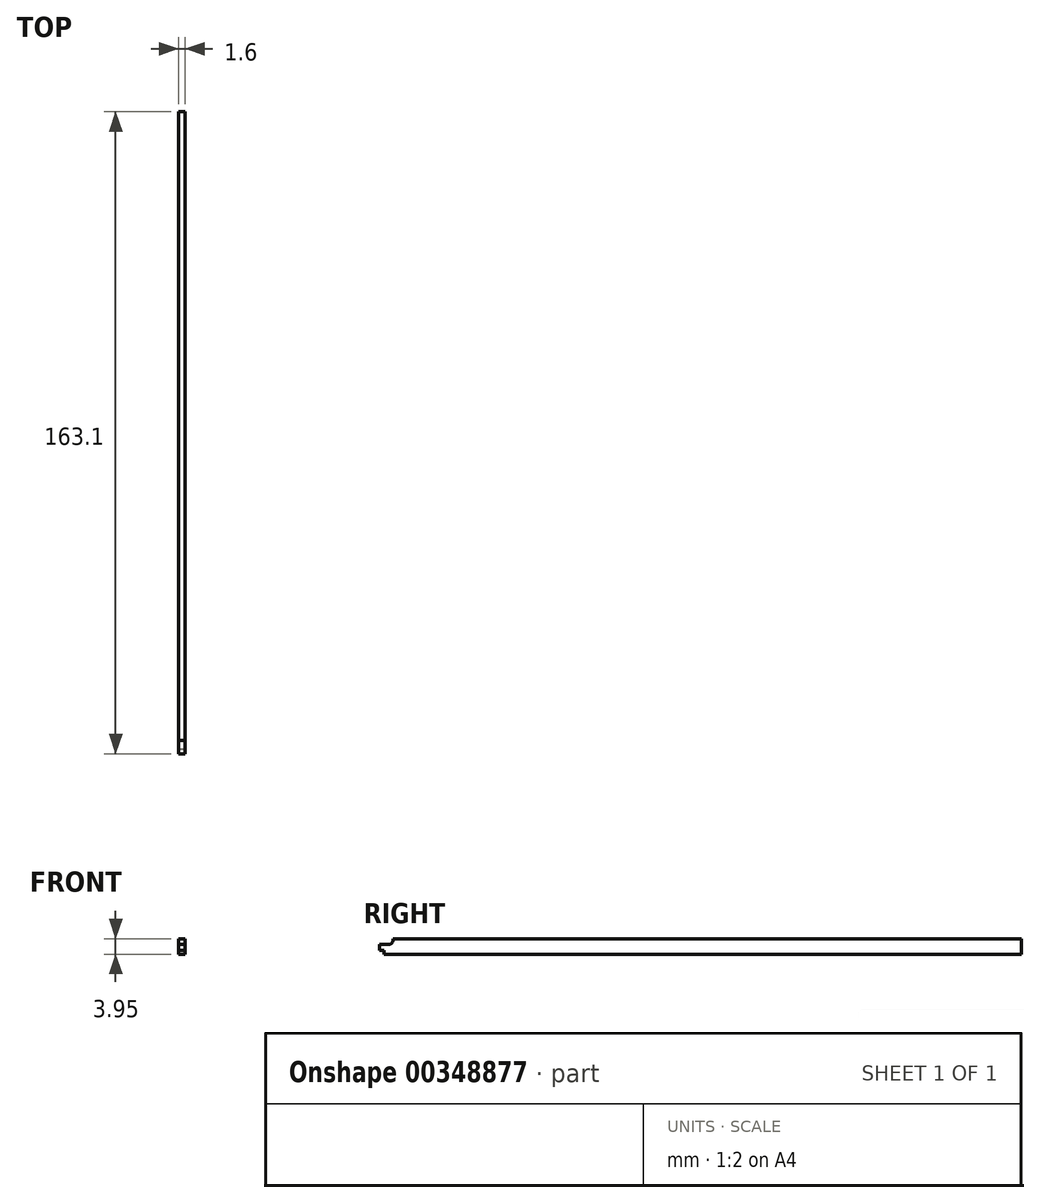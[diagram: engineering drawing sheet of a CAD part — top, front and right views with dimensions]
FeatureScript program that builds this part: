
annotation { "Feature Type Name" : "Feature", "Feature Type Description" : "" }
export const myFeature = defineFeature(function(context is Context, id is Id, definition is map)
    precondition{}
    {
        {
            var Q0;
            Q0=qCreatedBy(makeId("Front.planeOp"),FACE);
            var sketch = newSketch(context, id + "F0", { "sketchPlane" : qUnion([Q0])});
            skLineSegment(sketch, "E0.bottom", {"start": v(0, 0) * mm, "end": v(1.6, 0) * mm});
            skLineSegment(sketch, "E0.top", {"start": v(0, 3.95) * mm, "end": v(1.6, 3.95) * mm});
            skLineSegment(sketch, "E0.left", {"start": v(0, 0) * mm, "end": v(0, 3.95) * mm});
            skLineSegment(sketch, "E0.right", {"start": v(1.6, 0) * mm, "end": v(1.6, 3.95) * mm});
            skSolve(sketch);
        }
        {
            var Q0;
            Q0=qSketchRegion(id+"F0",true);
            extrude(context, id + "F1", {"entities" : qUnion([Q0]), "depth" : 163.1 * mm});
        }
        {
            var Q0;
            Q0=makeQuery(id+"F1.opExtrude","SWEPT_FACE",FACE,{"disambiguationData":[OSD([sQuery(id+"F0.wireOp",EDGE,"E0.right")])]});
            var sketch = newSketch(context, id + "F2", { "sketchPlane" : qUnion([Q0])});
            skLineSegment(sketch, "E1.bottom", {"start": v(-163.1, 3.95) * mm, "end": v(-159.7, 3.95) * mm});
            skLineSegment(sketch, "E1.top", {"start": v(-163.1, 2.5) * mm, "end": v(-160.7, 2.5) * mm});
            skLineSegment(sketch, "E1.left", {"start": v(-163.1, 3.95) * mm, "end": v(-163.1, 2.5) * mm});
            skLineSegment(sketch, "E1.right", {"start": v(-159.7, 3.95) * mm, "end": v(-159.7, 3.5) * mm});
            skLineSegment(sketch, "E2.bottom", {"start": v(-163.1, 0) * mm, "end": v(-161.9, 0) * mm});
            skLineSegment(sketch, "E2.top", {"start": v(-163.1, 1) * mm, "end": v(-161.9, 1) * mm});
            skLineSegment(sketch, "E2.left", {"start": v(-163.1, 0) * mm, "end": v(-163.1, 1) * mm});
            skLineSegment(sketch, "E2.right", {"start": v(-161.9, 0) * mm, "end": v(-161.9, 1) * mm});
            skPoint(sketch, "E3.visualSharp", {"position": v(-159.7, 2.5) * mm});
            skArc(sketch, "E3.filletArc", {"start": v(-160.7, 2.5) * mm, "mid": v(-160, 2.8) * mm, "end": v(-159.7, 3.5) * mm});
            skSolve(sketch);
        }
        {
            var Q0;
            Q0=qSketchRegion(id+"F2",true);
            extrude(context, id + "F3", {"entities" : qUnion([Q0]), "operationType" : NewBodyOperationType.REMOVE, "endBound" : BoundingType.THROUGH_ALL, "oppositeDirection" : true, "depth" : 25 * mm});
        }
    });
